# Revit family: agtatec_Record_SldngDrset_THERMCORD-D-STA_Standalone
name_source: partatom
category: Doors
revit_build: Autodesk Revit Architecture 2015 (Build: 20140606_1530(x64)
units: mm (PartAtom-declared; Revit-internal decimal feet)

## types (8) — shared parameters
AccessoryOptions = Contact manufacturer
AlternativeDoorsetGlazing = Part of glazing spec
AntiFingerTrapRequirement = Yes
Assembly Code = B2030110
BIMObjectName = agtatec_Record_SlidingDoorset_THERMCORD-D-STA_Standalone
CenterOfDoor = 1246 mm  [stored 4.08793 ft]
ClearHeightOfPassage = 2150 mm
Clearance Zones = No
ClearanceZoneLeft = 1246 mm  [stored 4.08793 ft]
ClearanceZoneRight = 1246 mm  [stored 4.08793 ft]
Colour = Customer specific
Configuration = 1 or 2
Construction Type = Automatic Sliding Door
Description = Automatic Sliding Door
DistanceToWall = 63 mm  [stored 0.206693 ft]
DoorIncluded = Yes
DoorsetFasteners = Screws
DoorsetOperation = Automatic
DriveDepth = 210 mm  [stored 0.688976 ft]
DriveUnit = agtatec_Record_Sliding Door, Sheet Metal (Painted Steel)
DriveUnitCenterDistance = 1246 mm  [stored 4.08793 ft]
DurationUnit = year
ElectronicLock = Yes
Finish = Powder coated, Anodized, customer specific
FireExit = No
FloorGuide = agtatec_Record_Sliding Door, Stainless Steel
FloorListDepth = 89 mm  [stored 0.291995 ft]
FrameMaterial = Aluminium
FrameProfile = Aluminium
FrameSeal = Yes
Function = Exterior
GlassLayers = 2
GlassThickness1 = 8 mm  [stored 0.0262467 ft]
GlassType = Part of glazing spec
HandicapAccessible = Yes
HasDrive = Yes
IfcExportAs = IfcDoorStyle
IfcExportType = Door
InnerPanelWidth = 646 mm  [stored 2.11942 ft]
InterlancingProfile2 = No
InterlancingProfile3 = Yes
InterlancingProfileHeight = 2195 mm  [stored 7.20144 ft]
IsExternal = Yes
LeafColourOptions = All RAL, customer specific
Manufacturer = Record
ManufacturerURL = www.agta-record.com
Material = Aluminium
Model = Thermcord D-STA
ModelReference = Depends on the configuration
MountingProfileLeft = No
MountingProfileRight = No
NBSDescription = Sliding Doorset
NBSReference = 25-50-20/175
Name = SldngDrset_THERMCORD-D-STA_Standalone_Record
OpeningWidth = 1200 mm
OuterPanelWidthLeft = 613.18 mm  [stored 2.01175 ft]
OuterPanelWidthRight = 613.18 mm  [stored 2.01175 ft]
PanelFill = agtatec_Record_Sliding Door, Laminated Safety Glass (Clear)
PanelFrames = agtatec_Record_Sliding Door, Aluminium
PanelHeight = 2200 mm
ProductInformation = www.agta-record.com
ReferenceStandard = EN16005, EN16361, DIN 18650, etc.
ReplacementCost = Depends on the configuration and door type
SelfClosing = Yes
ServiceLifeDuration = 10-15 years
Shape = Rectangular
SidePanelMinimumStandard = 646 mm  [stored 2.11942 ft]
SidePanelWidthLeft = 646 mm  [stored 2.11942 ft]
SidePanelWidthRight = 646 mm  [stored 2.11942 ft]
SmokeStop = No
SupportLength = 2492 mm  [stored 8.17585 ft]
ThresholdRequired = Yes
ThresholdStripping = No additional required, part of the doorset
URL = www.agta-record.com
Uniclass2 = Ss_25_30_20_77
Version = Version 1.0
WallMountingProfile = No
WarrantyDescription = Depends on country
WarrantyDurationLabour = Depends on country
WarrantyDurationParts = Depends on country
WarrantyDurationUnit = Depends on country
WarrantyGuarantorLabour = Local door manufacturer
WarrantyGuarantorParts = Local door manufacturer
Weight = Depends on configuration and size
WithDriveCladding = Yes
WithinStandardSizes = Yes
WithoutDriveCladding(OnlyApplicableForTypesWithoutSidePanels) = No
zero-valued in all types: Cost, DoorOpening, DoorOpeningRestriction, DriveUnitExtraWidthLeft, DriveUnitExtraWidthRight, ExtraLeft, ExtraRight, ExtraWidthLeft, ExtraWidthRight, GlassThickness2, NominalLength, ThermalTransmittance, Thickness

## per-type parameters (varying)
| type | DoorSeal | DriveUnitHeight | Height | InterlancingProfile1 | InterlancingProfileLeft | InterlancingProfileRight | LeftPanel | NominalHeight | NominalWidth | RightPanel | Rough Height | Rough Width | TotalHeight | TotalWidth | Wall Opening Width | Width | WithSidePanels | WithoutSidePanels |
| THERMCORD D-STA 150mm drive unit height with two side panels | yes | 150 mm | 2300 mm | Yes | No | No | Yes | 2300 mm | 2492 mm  [stored 8.17585 ft] | Yes | 2306 mm | 2498 mm  [stored 8.19554 ft] | 2300 mm | 2492 mm  [stored 8.17585 ft] | 2492 mm  [stored 8.17585 ft] | 2492 mm  [stored 8.17585 ft] | Yes | No |
| THERMCORD D-STA 150mm drive unit height side panel left | 1 | 150 mm | 2300 mm | Yes | No | Yes | Yes | 2300 mm | 1900.5 mm  [stored 6.23524 ft] | No | 2306 mm | 1906.5 mm  [stored 6.25492 ft] | 2300 mm | 1900.5 mm  [stored 6.23524 ft] | 1846 mm  [stored 6.05643 ft] | 1900.5 mm  [stored 6.23524 ft] | No | No |
| THERMCORD D-STA 150mm drive unit height side panel right | 1 | 150 mm | 2300 mm | Yes | Yes | No | No | 2300 mm | 1900.5 mm  [stored 6.23524 ft] | Yes | 2306 mm | 1906.5 mm  [stored 6.25492 ft] | 2300 mm | 1900.5 mm  [stored 6.23524 ft] | 1846 mm  [stored 6.05643 ft] | 1900.5 mm  [stored 6.23524 ft] | No | No |
| THERMCORD D-STA 150mm drive unit height without side panels | 1 | 150 mm | 2300 mm | No | Yes | Yes | No | 2300 mm | 1309 mm | No | 2306 mm | 1315 mm | 2300 mm | 1309 mm | 1200 mm | 1309 mm | No | Yes |
| THERMCORD D-STA 200mm drive unit height side panel left | 1 | 200 mm  [stored 0.656168 ft] | 2350 mm | Yes | No | Yes | Yes | 2350 mm | 1900.5 mm  [stored 6.23524 ft] | No | 2356 mm | 1906.5 mm  [stored 6.25492 ft] | 2350 mm | 1900.5 mm  [stored 6.23524 ft] | 1846 mm  [stored 6.05643 ft] | 1900.5 mm  [stored 6.23524 ft] | No | No |
| THERMCORD D-STA 200mm drive unit height side panel right | 1 | 200 mm  [stored 0.656168 ft] | 2350 mm | Yes | Yes | No | No | 2350 mm | 1900.5 mm  [stored 6.23524 ft] | Yes | 2356 mm | 1906.5 mm  [stored 6.25492 ft] | 2350 mm | 1900.5 mm  [stored 6.23524 ft] | 1846 mm  [stored 6.05643 ft] | 1900.5 mm  [stored 6.23524 ft] | No | No |
| THERMCORD D-STA 200mm drive unit height with two side panels | 1 | 200 mm  [stored 0.656168 ft] | 2350 mm | Yes | No | No | Yes | 2350 mm | 2492 mm  [stored 8.17585 ft] | Yes | 2356 mm | 2498 mm  [stored 8.19554 ft] | 2350 mm | 2492 mm  [stored 8.17585 ft] | 2492 mm  [stored 8.17585 ft] | 2492 mm  [stored 8.17585 ft] | Yes | No |
| THERMCORD D-STA 200mm drive unit height without side panels | 1 | 200 mm  [stored 0.656168 ft] | 2350 mm | No | Yes | Yes | No | 2350 mm | 1309 mm | No | 2356 mm | 1315 mm | 2350 mm | 1309 mm | 1200 mm | 1309 mm | No | Yes |

note: [stored X ft] marks values corroborated as IEEE doubles in the binary element streams (Revit-internal decimal feet)

## geometry (parser evidence)
native form markers: Sweep x10
no freeform markers — native parametric forms only
